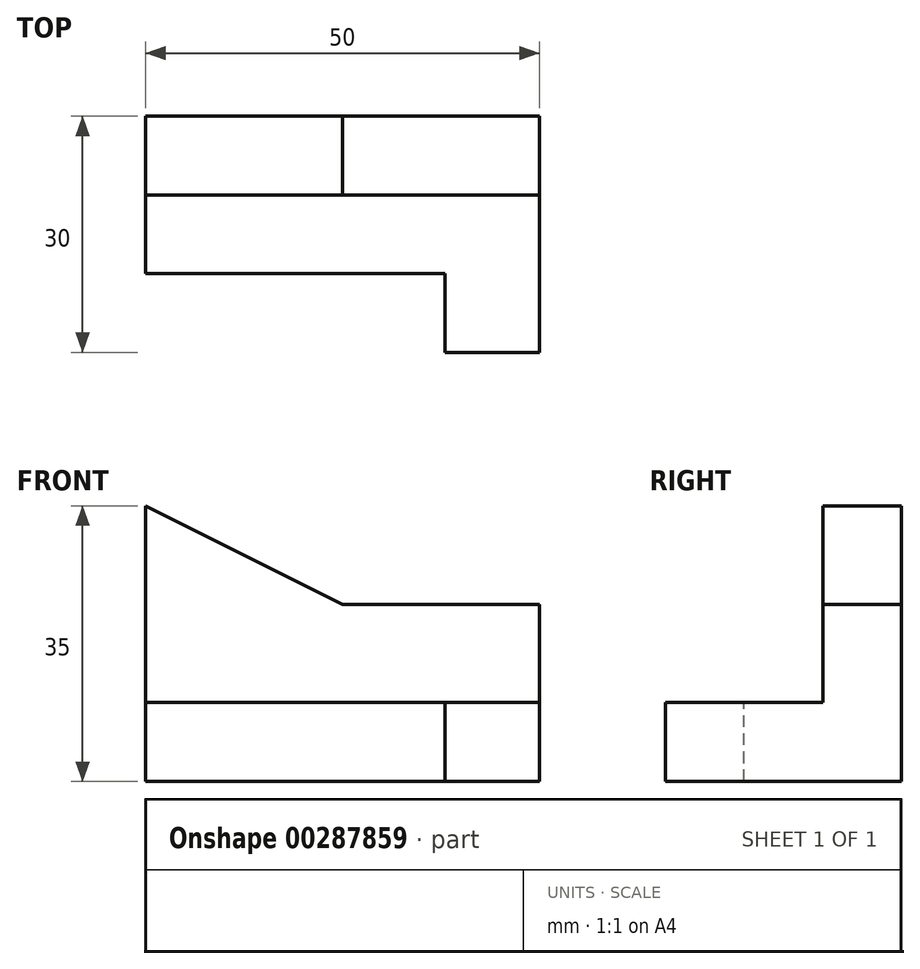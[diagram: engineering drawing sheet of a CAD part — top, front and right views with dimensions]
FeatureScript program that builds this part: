
annotation { "Feature Type Name" : "Feature", "Feature Type Description" : "" }
export const myFeature = defineFeature(function(context is Context, id is Id, definition is map)
    precondition{}
    {
        {
            var Q0;
            Q0=qCreatedBy(makeId("Front.planeOp"),FACE);
            var sketch = newSketch(context, id + "F0", { "sketchPlane" : qUnion([Q0])});
            skLineSegment(sketch, "E0.bottom", {"start": v(0, 0) * mm, "end": v(50, 0) * mm});
            skLineSegment(sketch, "E0.top", {"start": v(0, 35) * mm, "end": v(50, 35) * mm});
            skLineSegment(sketch, "E0.left", {"start": v(0, 0) * mm, "end": v(0, 35) * mm});
            skLineSegment(sketch, "E0.right", {"start": v(50, 0) * mm, "end": v(50, 35) * mm});
            skSolve(sketch);
        }
        {
            var Q0;
            Q0 = qSketchRegion(id + "F0", true);
            extrude(context, id + "F1", {"entities" : qUnion([Q0]), "depth" : 30 * mm});
        }
        {
            var Q0;
            Q0=makeQuery(id+"F1.opExtrude","SWEPT_FACE",FACE,{"disambiguationData":[OSD([sQuery(id+"F0.wireOp",EDGE,"E0.right")])]});
            var sketch = newSketch(context, id + "F2", { "sketchPlane" : qUnion([Q0])});
            skLineSegment(sketch, "E1.bottom", {"start": v(-30, 35) * mm, "end": v(-10, 35) * mm});
            skLineSegment(sketch, "E1.top", {"start": v(-30, 10) * mm, "end": v(-10, 10) * mm});
            skLineSegment(sketch, "E1.left", {"start": v(-30, 35) * mm, "end": v(-30, 10) * mm});
            skLineSegment(sketch, "E1.right", {"start": v(-10, 35) * mm, "end": v(-10, 10) * mm});
            skSolve(sketch);
        }
        {
            var Q0;
            Q0 = qSketchRegion(id + "F2", true);
            extrude(context, id + "F3", {"entities" : qUnion([Q0]), "operationType" : NewBodyOperationType.REMOVE, "endBound" : BoundingType.THROUGH_ALL, "oppositeDirection" : true, "depth" : 25 * mm});
        }
        {
            var Q0;
            Q0=makeQuery(id+"F3.boolean.opBoolean","COPY",FACE,{"derivedFrom":makeQuery(id+"F3.opExtrude","SWEPT_FACE",FACE,{"disambiguationData":[OSD([sQuery(id+"F2.wireOp",EDGE,"E1.top")])]})});
            var sketch = newSketch(context, id + "F4", { "sketchPlane" : qUnion([Q0])});
            skLineSegment(sketch, "E2.bottom", {"start": v(0, -30) * mm, "end": v(38, -30) * mm});
            skLineSegment(sketch, "E2.top", {"start": v(0, -20) * mm, "end": v(38, -20) * mm});
            skLineSegment(sketch, "E2.left", {"start": v(0, -30) * mm, "end": v(0, -20) * mm});
            skLineSegment(sketch, "E2.right", {"start": v(38, -30) * mm, "end": v(38, -20) * mm});
            skSolve(sketch);
        }
        {
            var Q0;
            Q0 = qSketchRegion(id + "F4", true);
            extrude(context, id + "F5", {"entities" : qUnion([Q0]), "operationType" : NewBodyOperationType.REMOVE, "endBound" : BoundingType.THROUGH_ALL, "oppositeDirection" : true, "depth" : 25 * mm});
        }
        {
            var Q0;
            Q0=makeQuery(id+"F3.boolean.opBoolean","COPY",FACE,{"derivedFrom":makeQuery(id+"F3.opExtrude","SWEPT_FACE",FACE,{"disambiguationData":[OSD([sQuery(id+"F2.wireOp",EDGE,"E1.right")])]})});
            var sketch = newSketch(context, id + "F6", { "sketchPlane" : qUnion([Q0])});
            skLineSegment(sketch, "E3", {"start": v(0, 35) * mm, "end": v(25, 22.5) * mm});
            skPoint(sketch, "E3.endSnap0", {"position": v(50, 22.5) * mm});
            skPoint(sketch, "E3.endSnap1", {"position": v(25, 35) * mm});
            skLineSegment(sketch, "E4", {"start": v(25, 22.5) * mm, "end": v(50, 22.5) * mm});
            skLineSegment(sketch, "E5.0", {"start": v(0, 35) * mm, "end": v(50, 35) * mm});
            skLineSegment(sketch, "E6.0", {"start": v(50, 35) * mm, "end": v(50, 10) * mm});
            skSolve(sketch);
        }
        {
            var Q0;
            Q0 = qSketchRegion(id + "F6", true);
            extrude(context, id + "F7", {"entities" : qUnion([Q0]), "operationType" : NewBodyOperationType.REMOVE, "endBound" : BoundingType.THROUGH_ALL, "oppositeDirection" : true, "depth" : 25 * mm});
        }
    });
